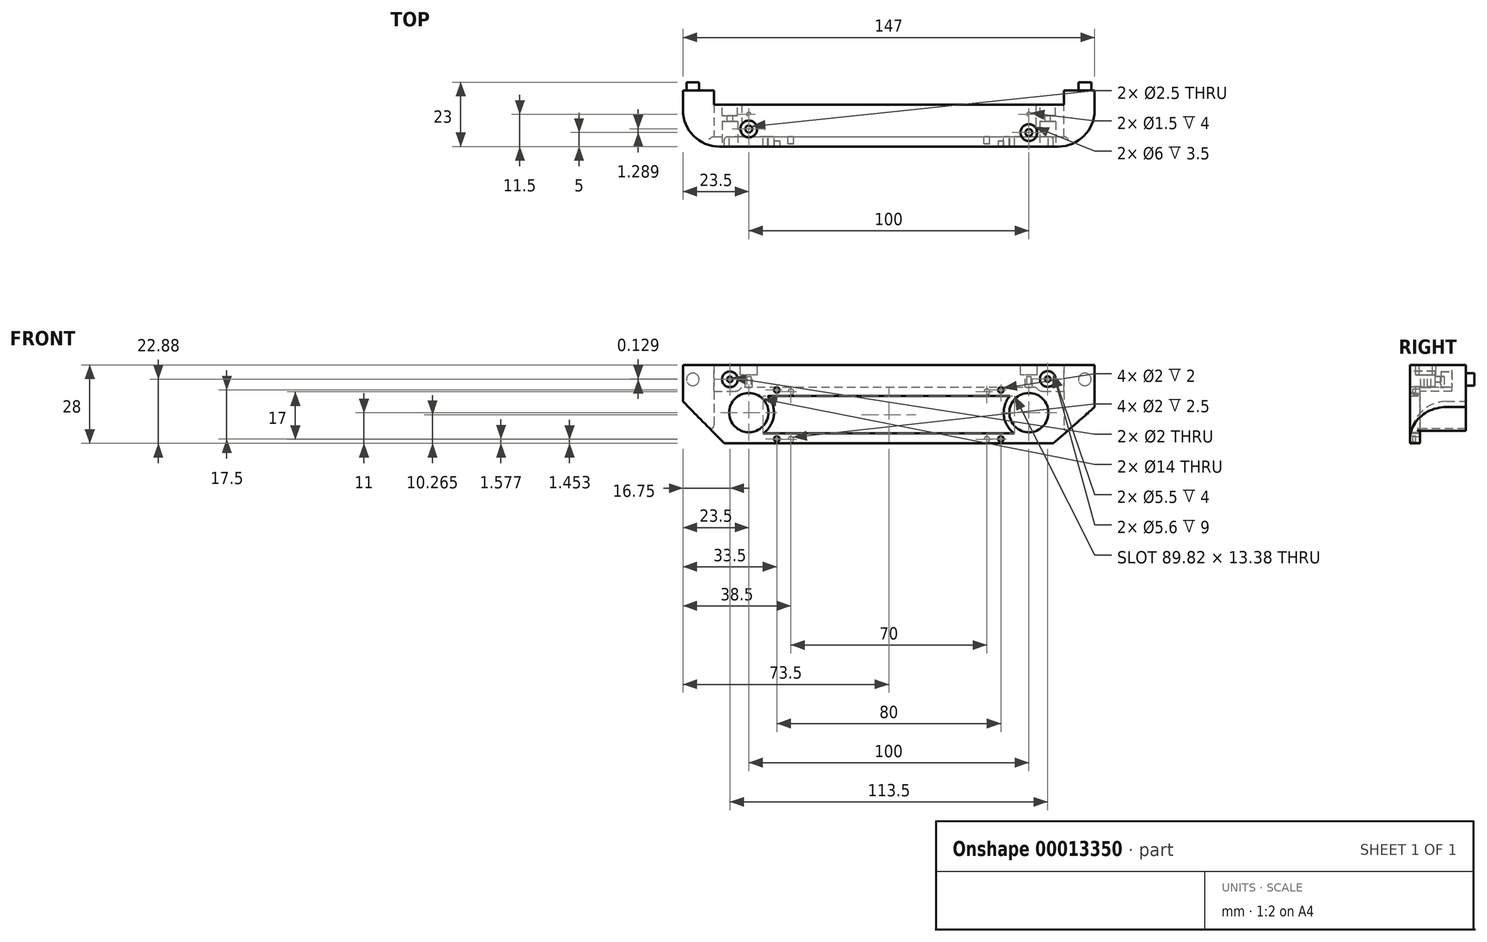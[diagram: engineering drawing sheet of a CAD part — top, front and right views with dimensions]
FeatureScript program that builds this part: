
annotation { "Feature Type Name" : "Feature", "Feature Type Description" : "" }
export const myFeature = defineFeature(function(context is Context, id is Id, definition is map)
    precondition{}
    {
        {
            var Q0;
            Q0=qCreatedBy(makeId("Front.planeOp"),FACE);
            var sketch = newSketch(context, id + "F0", { "sketchPlane" : qUnion([Q0])});
            skLineSegment(sketch, "E0.bottom", {"start": v(-73.5, 15) * mm, "end": v(73.5, 15) * mm});
            skLineSegment(sketch, "E0.top", {"start": v(-58.75, -13) * mm, "end": v(58.75, -13) * mm});
            skCircle(sketch, "E1", {"center": v(-50, -2) * mm, "radius": 7 * mm});
            skCircle(sketch, "E2", {"center": v(50, -2) * mm, "radius": 7 * mm});
            skArc(sketch, "E3", {"start": v(-44.91, -9.42) * mm, "mid": v(-41.07, -3.1) * mm, "end": v(-43.25, 3.95) * mm});
            skArc(sketch, "E4", {"start": v(43.25, 3.95) * mm, "mid": v(41.07, -3.1) * mm, "end": v(44.91, -9.42) * mm});
            skLineSegment(sketch, "E5.bottom", {"start": v(-44.91, -9.42) * mm, "end": v(45.08, -9.42) * mm});
            skLineSegment(sketch, "E5.top", {"start": v(-43.25, 3.95) * mm, "end": v(43.25, 3.95) * mm});
            skCircle(sketch, "E6", {"center": v(-56.75, 9.88) * mm, "radius": 1 * mm});
            skCircle(sketch, "E7", {"center": v(56.75, 10) * mm, "radius": 1 * mm});
            skPoint(sketch, "E8.orphan", {"position": v(56.75, 3.95) * mm});
            skPoint(sketch, "E9.second.point", {"position": v(-69.33, 5.65) * mm});
            skPoint(sketch, "E9.third.point", {"position": v(-64.18, 7.48) * mm});
            skPoint(sketch, "E10.first.point", {"position": v(69.33, 5.65) * mm});
            skPoint(sketch, "E10.third.point", {"position": v(64.2, 14.68) * mm});
            skLineSegment(sketch, "E11.bottom", {"start": v(-73.5, 15) * mm, "end": v(-66.12, 15) * mm});
            skLineSegment(sketch, "E11.left", {"start": v(-73.5, 15) * mm, "end": v(-73.5, 2) * mm});
            skLineSegment(sketch, "E12.bottom", {"start": v(73.5, 15) * mm, "end": v(66.13, 15) * mm});
            skLineSegment(sketch, "E12.left", {"start": v(73.5, 15) * mm, "end": v(73.5, 0) * mm});
            skLineSegment(sketch, "E13", {"start": v(-73.5, 2) * mm, "end": v(-58.75, -13) * mm});
            skPoint(sketch, "E14.end.orphan", {"position": v(-66.12, 0) * mm});
            skLineSegment(sketch, "E15", {"start": v(58.75, -13) * mm, "end": v(73.5, 0) * mm});
            skPoint(sketch, "E16.end.orphan", {"position": v(66.12, 0) * mm});
            skSolve(sketch);
        }
        {
            var Q0;
            Q0 = qSketchRegion(id + "F0", true);
            extrude(context, id + "F1", {"entities" : qUnion([Q0]), "depth" : 20 * mm});
        }
        {
            var Q0;
            Q0=qCreatedBy(makeId("Right.planeOp"),FACE);
            var sketch = newSketch(context, id + "F2", { "sketchPlane" : qUnion([Q0])});
            skLineSegment(sketch, "E17.bottom", {"start": v(0, 5.65) * mm, "end": v(-16.5, 5.65) * mm});
            skLineSegment(sketch, "E17.top", {"start": v(0, -13) * mm, "end": v(-16.5, -13) * mm});
            skLineSegment(sketch, "E17.left", {"start": v(0, 5.65) * mm, "end": v(0, -13) * mm});
            skLineSegment(sketch, "E17.right", {"start": v(-16.5, 5.65) * mm, "end": v(-16.5, -13) * mm});
            skSolve(sketch);
        }
        {
            var Q0;
            Q0 = qSketchRegion(id + "F2", true);
            extrude(context, id + "F3", {"entities" : qUnion([Q0]), "operationType" : NewBodyOperationType.REMOVE, "endBound" : BoundingType.SYMMETRIC, "oppositeDirection" : true, "depth" : 125 * mm});
        }
        {
            var Q0;
            Q0=makeQuery(id+"F1.opExtrude","SWEPT_FACE",FACE,{"disambiguationData":[OSD([sQuery(id+"F0.wireOp",EDGE,"E0.bottom")])]});
            var sketch = newSketch(context, id + "F4", { "sketchPlane" : qUnion([Q0])});
            skLineSegment(sketch, "E18.bottom", {"start": v(-62.5, 9.15) * mm, "end": v(62.5, 9.15) * mm});
            skLineSegment(sketch, "E18.top", {"start": v(-62.5, -5) * mm, "end": v(62.5, -5) * mm});
            skLineSegment(sketch, "E18.left", {"start": v(-62.5, 9.15) * mm, "end": v(-62.5, -5) * mm});
            skLineSegment(sketch, "E18.right", {"start": v(62.5, 9.15) * mm, "end": v(62.5, -5) * mm});
            skSolve(sketch);
        }
        {
            var Q0;
            Q0 = qSketchRegion(id + "F4", true);
            extrude(context, id + "F5", {"entities" : qUnion([Q0]), "operationType" : NewBodyOperationType.REMOVE, "oppositeDirection" : true, "depth" : 25 * mm});
        }
        {
            var Q0;
            Q0=makeQuery(id+"F5.boolean.opBoolean","COPY",FACE,{"derivedFrom":makeQuery(id+"F5.opExtrude","SWEPT_FACE",FACE,{"disambiguationData":[OSD([sQuery(id+"F4.wireOp",EDGE,"E18.top")])]})});
            var sketch = newSketch(context, id + "F6", { "sketchPlane" : qUnion([Q0])});
            skCircle(sketch, "E19", {"center": v(-56.75, 10) * mm, "radius": 2.75 * mm});
            skCircle(sketch, "E20", {"center": v(56.75, 9.88) * mm, "radius": 2.75 * mm});
            skSolve(sketch);
        }
        {
            var Q0;
            Q0 = qSketchRegion(id + "F6", true);
            extrude(context, id + "F7", {"entities" : qUnion([Q0]), "operationType" : NewBodyOperationType.REMOVE, "oppositeDirection" : true, "depth" : 4 * mm});
        }
        {
            var Q0;
            {var subQ0=sQuery(id+"F0.wireOp",EDGE,"E0.bottom");var subQ1=sQuery(id+"F0.wireOp",EDGE,"E11.bottom");var subQ2=sQuery(id+"F0.wireOp",EDGE,"E12.bottom");var subQ3=sQuery(id+"F0.wireOp",EDGE,"E12.left");Q0=makeQuery(id+"F5.boolean.opBoolean","SPLIT",FACE,{"disambiguationData":[TD([makeQuery(id+"F1.opExtrude","SWEPT_FACE",FACE,{"disambiguationData":[OSD([subQ3])]})])],"derivedFrom":makeQuery(id+"F1.opExtrude","CAP_FACE",FACE,{"disambiguationData":[OSD([subQ0,sQuery(id+"F0.wireOp",EDGE,"E0.top"),sQuery(id+"F0.wireOp",EDGE,"E1"),sQuery(id+"F0.wireOp",EDGE,"E2"),sQuery(id+"F0.wireOp",EDGE,"E3"),sQuery(id+"F0.wireOp",EDGE,"E4"),sQuery(id+"F0.wireOp",EDGE,"E5.bottom"),sQuery(id+"F0.wireOp",EDGE,"E5.top"),sQuery(id+"F0.wireOp",EDGE,"E6"),sQuery(id+"F0.wireOp",EDGE,"E7"),subQ1,sQuery(id+"F0.wireOp",EDGE,"E11.left"),subQ2,subQ3,sQuery(id+"F0.wireOp",EDGE,"E13"),sQuery(id+"F0.wireOp",EDGE,"E15")])],"isStart":true})});}
            var sketch = newSketch(context, id + "F8", { "sketchPlane" : qUnion([Q0])});
            skCircle(sketch, "E21", {"center": v(-70, 9.88) * mm, "radius": 2.25 * mm});
            skCircle(sketch, "E22", {"center": v(70, 9.88) * mm, "radius": 2.25 * mm});
            skSolve(sketch);
        }
        {
            var Q0;
            Q0 = qSketchRegion(id + "F8", true);
            extrude(context, id + "F9", {"entities" : qUnion([Q0]), "operationType" : NewBodyOperationType.ADD, "depth" : 3 * mm});
        }
        {
            var Q0;
            Q0=makeQuery(id+"F1.opExtrude","CAP_FACE",FACE,{"disambiguationData":[OSD([sQuery(id+"F0.wireOp",EDGE,"E0.bottom"),sQuery(id+"F0.wireOp",EDGE,"E0.top"),sQuery(id+"F0.wireOp",EDGE,"E1"),sQuery(id+"F0.wireOp",EDGE,"E2"),sQuery(id+"F0.wireOp",EDGE,"E3"),sQuery(id+"F0.wireOp",EDGE,"E4"),sQuery(id+"F0.wireOp",EDGE,"E5.bottom"),sQuery(id+"F0.wireOp",EDGE,"E5.top"),sQuery(id+"F0.wireOp",EDGE,"E6"),sQuery(id+"F0.wireOp",EDGE,"E7"),sQuery(id+"F0.wireOp",EDGE,"E11.bottom"),sQuery(id+"F0.wireOp",EDGE,"E11.left"),sQuery(id+"F0.wireOp",EDGE,"E12.bottom"),sQuery(id+"F0.wireOp",EDGE,"E12.left"),sQuery(id+"F0.wireOp",EDGE,"E13"),sQuery(id+"F0.wireOp",EDGE,"E15")])],"isStart":false});
            var sketch = newSketch(context, id + "F10", { "sketchPlane" : qUnion([Q0])});
            skCircle(sketch, "E23", {"center": v(-56.75, 9.88) * mm, "radius": 2.8 * mm});
            skCircle(sketch, "E24", {"center": v(56.75, 10) * mm, "radius": 2.8 * mm});
            skSolve(sketch);
        }
        {
            var Q0;
            Q0 = qSketchRegion(id + "F10", true);
            extrude(context, id + "F11", {"entities" : qUnion([Q0]), "operationType" : NewBodyOperationType.REMOVE, "oppositeDirection" : true, "depth" : 9 * mm});
        }
        {
            var Q0;
            Q0=makeQuery(id+"F1.opExtrude","CAP_EDGE",EDGE,{"disambiguationData":[OSD([sQuery(id+"F0.wireOp",EDGE,"E11.left")])],"isStart":false});
            var Q1;
            Q1=makeQuery(id+"F1.opExtrude","CAP_EDGE",EDGE,{"disambiguationData":[OSD([sQuery(id+"F0.wireOp",EDGE,"E12.left")])],"isStart":false});
            fillet(context, id + "F12", {"entities" : qUnion([Q0, Q1]), "radius" : 13 * mm, "tangentPropagation" : true, "allowEdgeOverflow" : false});
        }
        {
            var Q0;
            Q0=qCreatedBy(makeId("Right.planeOp"),FACE);
            var sketch = newSketch(context, id + "F13", { "sketchPlane" : qUnion([Q0])});
            skLineSegment(sketch, "E25.bottom", {"start": v(0, 0) * mm, "end": v(-16.5, 0) * mm});
            skLineSegment(sketch, "E25.top", {"start": v(0, 7) * mm, "end": v(-16.5, 7) * mm});
            skLineSegment(sketch, "E25.left", {"start": v(0, 0) * mm, "end": v(0, 7) * mm});
            skLineSegment(sketch, "E25.right", {"start": v(-16.5, 0) * mm, "end": v(-16.5, 7) * mm});
            skSolve(sketch);
        }
        {
            var Q0;
            Q0 = qSketchRegion(id + "F13", true);
            extrude(context, id + "F14", {"entities" : qUnion([Q0]), "operationType" : NewBodyOperationType.REMOVE, "endBound" : BoundingType.SYMMETRIC, "oppositeDirection" : true, "depth" : 105 * mm});
        }
        {
            var Q0;
            Q0=makeQuery(id+"F14.boolean.opBoolean","INTERSECT",EDGE,{"derivedFrom":[makeQuery(id+"F3.boolean.opBoolean","COPY",FACE,{"derivedFrom":makeQuery(id+"F3.opExtrude","SWEPT_FACE",FACE,{"disambiguationData":[OSD([sQuery(id+"F2.wireOp",EDGE,"E17.bottom")])]})}),makeQuery(id+"F14.opExtrude","CAP_FACE",FACE,{"disambiguationData":[OSD([sQuery(id+"F13.wireOp",EDGE,"E25.bottom"),sQuery(id+"F13.wireOp",EDGE,"E25.top"),sQuery(id+"F13.wireOp",EDGE,"E25.left"),sQuery(id+"F13.wireOp",EDGE,"E25.right")])],"isStart":true})]});
            var Q1;
            Q1=makeQuery(id+"F14.boolean.opBoolean","INTERSECT",EDGE,{"derivedFrom":[makeQuery(id+"F3.boolean.opBoolean","COPY",FACE,{"derivedFrom":makeQuery(id+"F3.opExtrude","SWEPT_FACE",FACE,{"disambiguationData":[OSD([sQuery(id+"F2.wireOp",EDGE,"E17.bottom")])]})}),makeQuery(id+"F14.opExtrude","CAP_FACE",FACE,{"disambiguationData":[OSD([sQuery(id+"F13.wireOp",EDGE,"E25.bottom"),sQuery(id+"F13.wireOp",EDGE,"E25.top"),sQuery(id+"F13.wireOp",EDGE,"E25.left"),sQuery(id+"F13.wireOp",EDGE,"E25.right")])],"isStart":false})]});
            fillet(context, id + "F15", {"entities" : qUnion([Q0, Q1]), "radius" : 3 * mm, "tangentPropagation" : true, "allowEdgeOverflow" : false});
        }
        {
            var Q0;
            Q0=makeQuery(id+"F1.opExtrude","SWEPT_FACE",FACE,{"disambiguationData":[OSD([sQuery(id+"F0.wireOp",EDGE,"E0.bottom"),sQuery(id+"F0.wireOp",EDGE,"E11.bottom"),sQuery(id+"F0.wireOp",EDGE,"E12.bottom")])]});
            var sketch = newSketch(context, id + "F16", { "sketchPlane" : qUnion([Q0])});
            skCircle(sketch, "E26", {"center": v(50, -15) * mm, "radius": 1.25 * mm});
            skCircle(sketch, "E27", {"center": v(-50, -13.71) * mm, "radius": 1.25 * mm});
            skSolve(sketch);
        }
        {
            var Q0;
            Q0 = qSketchRegion(id + "F16", true);
            extrude(context, id + "F17", {"entities" : qUnion([Q0]), "operationType" : NewBodyOperationType.REMOVE, "endBound" : BoundingType.THROUGH_ALL, "oppositeDirection" : true, "depth" : 25 * mm});
        }
        {
            var Q0;
            Q0=makeQuery(id+"F14.boolean.opBoolean","COPY",FACE,{"derivedFrom":makeQuery(id+"F14.opExtrude","SWEPT_FACE",FACE,{"disambiguationData":[OSD([sQuery(id+"F13.wireOp",EDGE,"E25.top")])]})});
            var sketch = newSketch(context, id + "F18", { "sketchPlane" : qUnion([Q0])});
            skCircle(sketch, "E28", {"center": v(50, 8.5) * mm, "radius": 0.75 * mm});
            skCircle(sketch, "E29", {"center": v(-50, 8.5) * mm, "radius": 0.75 * mm});
            skSolve(sketch);
        }
        {
            var Q0;
            Q0 = qSketchRegion(id + "F18", true);
            extrude(context, id + "F19", {"entities" : qUnion([Q0]), "operationType" : NewBodyOperationType.REMOVE, "oppositeDirection" : true, "depth" : 4 * mm});
        }
        {
            var Q0;
            Q0=makeQuery(id+"F1.opExtrude","SWEPT_FACE",FACE,{"disambiguationData":[OSD([sQuery(id+"F0.wireOp",EDGE,"E0.bottom"),sQuery(id+"F0.wireOp",EDGE,"E11.bottom"),sQuery(id+"F0.wireOp",EDGE,"E12.bottom")])]});
            var sketch = newSketch(context, id + "F20", { "sketchPlane" : qUnion([Q0])});
            skCircle(sketch, "E30", {"center": v(-50, -13.71) * mm, "radius": 3 * mm});
            skCircle(sketch, "E31", {"center": v(50, -15) * mm, "radius": 3 * mm});
            skSolve(sketch);
        }
        {
            var Q0;
            Q0 = qSketchRegion(id + "F20", true);
            extrude(context, id + "F21", {"entities" : qUnion([Q0]), "operationType" : NewBodyOperationType.REMOVE, "oppositeDirection" : true, "depth" : 3.5 * mm});
        }
        {
            var Q0;
            Q0=makeQuery(id+"F1.opExtrude","CAP_FACE",FACE,{"disambiguationData":[OSD([sQuery(id+"F0.wireOp",EDGE,"E0.bottom"),sQuery(id+"F0.wireOp",EDGE,"E0.top"),sQuery(id+"F0.wireOp",EDGE,"E1"),sQuery(id+"F0.wireOp",EDGE,"E2"),sQuery(id+"F0.wireOp",EDGE,"E3"),sQuery(id+"F0.wireOp",EDGE,"E4"),sQuery(id+"F0.wireOp",EDGE,"E5.bottom"),sQuery(id+"F0.wireOp",EDGE,"E5.top"),sQuery(id+"F0.wireOp",EDGE,"E6"),sQuery(id+"F0.wireOp",EDGE,"E7"),sQuery(id+"F0.wireOp",EDGE,"E11.bottom"),sQuery(id+"F0.wireOp",EDGE,"E11.left"),sQuery(id+"F0.wireOp",EDGE,"E12.bottom"),sQuery(id+"F0.wireOp",EDGE,"E12.left"),sQuery(id+"F0.wireOp",EDGE,"E13"),sQuery(id+"F0.wireOp",EDGE,"E15")])],"isStart":false});
            var sketch = newSketch(context, id + "F22", { "sketchPlane" : qUnion([Q0])});
            skCircle(sketch, "E32", {"center": v(-40, 6.08) * mm, "radius": 1 * mm});
            skCircle(sketch, "E33", {"center": v(-40, -11.42) * mm, "radius": 1 * mm});
            skCircle(sketch, "E34", {"center": v(40, 6.08) * mm, "radius": 1 * mm});
            skCircle(sketch, "E35", {"center": v(40, -11.42) * mm, "radius": 1 * mm});
            skSolve(sketch);
        }
        {
            var Q0;
            Q0 = qSketchRegion(id + "F22", true);
            extrude(context, id + "F23", {"entities" : qUnion([Q0]), "operationType" : NewBodyOperationType.REMOVE, "oppositeDirection" : true, "depth" : 2 * mm});
        }
        {
            var Q0;
            Q0=qCreatedBy(makeId("Front.planeOp"),FACE);
            var sketch = newSketch(context, id + "F24", { "sketchPlane" : qUnion([Q0])});
            skCircle(sketch, "E36", {"center": v(-35, -11.55) * mm, "radius": 1 * mm});
            skCircle(sketch, "E37", {"center": v(-35, 5.45) * mm, "radius": 1 * mm});
            skCircle(sketch, "E38", {"center": v(35, 5.45) * mm, "radius": 1 * mm});
            skCircle(sketch, "E39", {"center": v(35, -11.55) * mm, "radius": 1 * mm});
            skSolve(sketch);
        }
        {
            var Q0;
            Q0 = qSketchRegion(id + "F24", true);
            extrude(context, id + "F25", {"entities" : qUnion([Q0]), "operationType" : NewBodyOperationType.REMOVE, "depth" : 19 * mm});
        }
        {
            var Q0;
            Q0=makeQuery(id+"F3.boolean.opBoolean","INTERSECT",EDGE,{"derivedFrom":[makeQuery(id+"F1.opExtrude","SWEPT_FACE",FACE,{"disambiguationData":[OSD([sQuery(id+"F0.wireOp",EDGE,"E13")])]}),makeQuery(id+"F3.opExtrude","CAP_FACE",FACE,{"disambiguationData":[OSD([sQuery(id+"F2.wireOp",EDGE,"E17.bottom"),sQuery(id+"F2.wireOp",EDGE,"E17.top"),sQuery(id+"F2.wireOp",EDGE,"E17.left"),sQuery(id+"F2.wireOp",EDGE,"E17.right")])],"isStart":false})]});
            var Q1;
            Q1=makeQuery(id+"F3.boolean.opBoolean","INTERSECT",EDGE,{"derivedFrom":[makeQuery(id+"F1.opExtrude","SWEPT_FACE",FACE,{"disambiguationData":[OSD([sQuery(id+"F0.wireOp",EDGE,"E13")])]}),makeQuery(id+"F3.opExtrude","SWEPT_FACE",FACE,{"disambiguationData":[OSD([sQuery(id+"F2.wireOp",EDGE,"E17.right")])]})]});
            var Q2;
            Q2=makeQuery(id+"F3.boolean.opBoolean","INTERSECT",EDGE,{"derivedFrom":[makeQuery(id+"F1.opExtrude","SWEPT_FACE",FACE,{"disambiguationData":[OSD([sQuery(id+"F0.wireOp",EDGE,"E15")])]}),makeQuery(id+"F3.opExtrude","CAP_FACE",FACE,{"disambiguationData":[OSD([sQuery(id+"F2.wireOp",EDGE,"E17.bottom"),sQuery(id+"F2.wireOp",EDGE,"E17.top"),sQuery(id+"F2.wireOp",EDGE,"E17.left"),sQuery(id+"F2.wireOp",EDGE,"E17.right")])],"isStart":true})]});
            var Q3;
            Q3=makeQuery(id+"F3.boolean.opBoolean","INTERSECT",EDGE,{"derivedFrom":[makeQuery(id+"F1.opExtrude","SWEPT_FACE",FACE,{"disambiguationData":[OSD([sQuery(id+"F0.wireOp",EDGE,"E15")])]}),makeQuery(id+"F3.opExtrude","SWEPT_FACE",FACE,{"disambiguationData":[OSD([sQuery(id+"F2.wireOp",EDGE,"E17.right")])]})]});
            fillet(context, id + "F26", {"entities" : qUnion([Q0, Q1, Q2, Q3]), "radius" : 1 * mm, "tangentPropagation" : true, "allowEdgeOverflow" : false});
        }
    });
